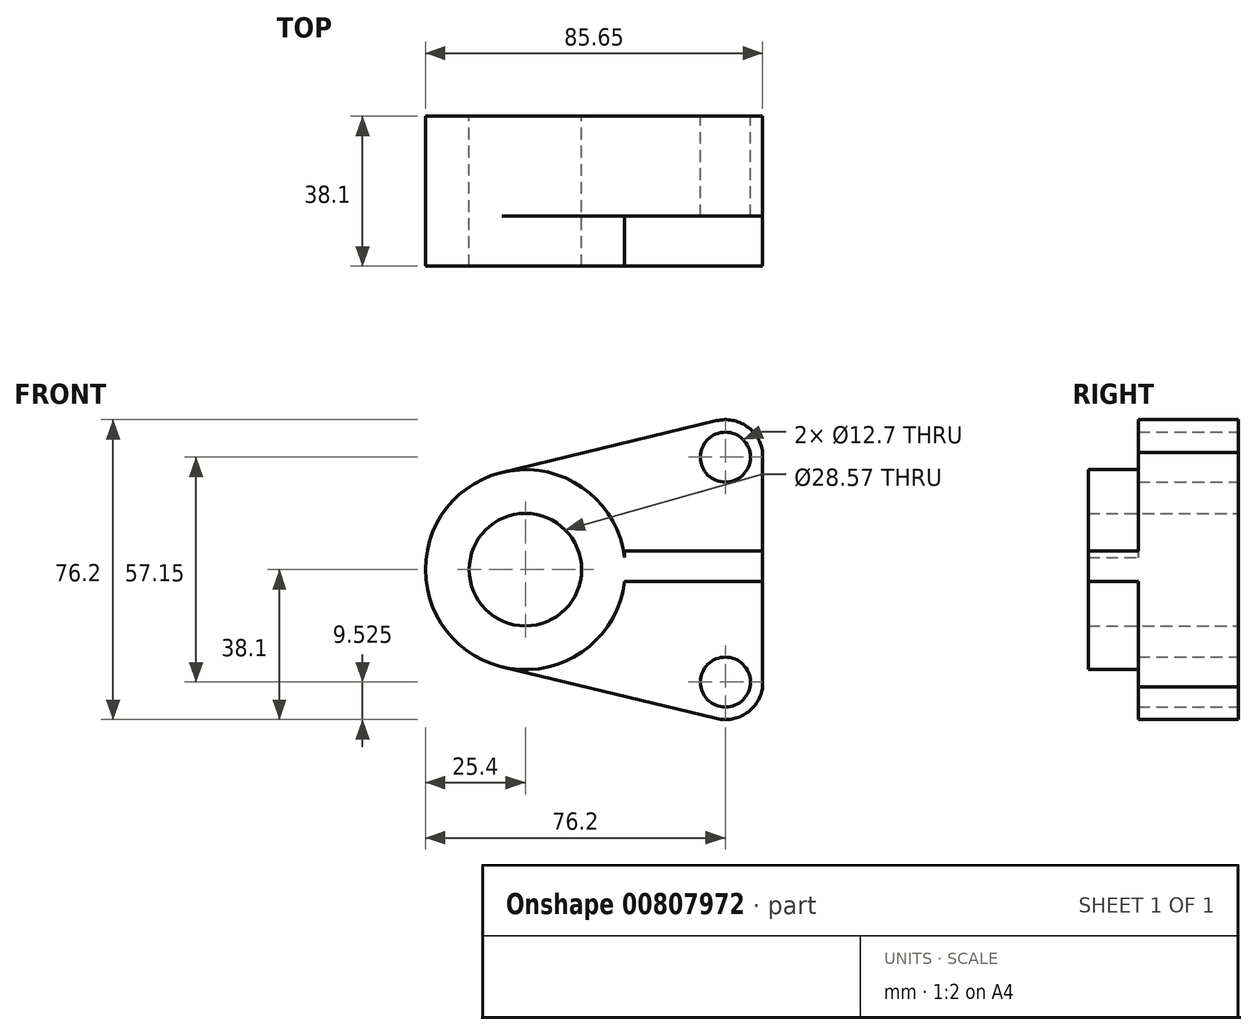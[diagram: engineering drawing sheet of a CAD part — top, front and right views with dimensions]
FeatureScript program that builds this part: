
annotation { "Feature Type Name" : "Feature", "Feature Type Description" : "" }
export const myFeature = defineFeature(function(context is Context, id is Id, definition is map)
    precondition{}
    {
        {
            var Q0;
            Q0=qCreatedBy(makeId("Front.planeOp"),FACE);
            var sketch = newSketch(context, id + "F0", { "sketchPlane" : qUnion([Q0])});
            skCircle(sketch, "E0", {"center": v(0, 0) * mm, "radius": 14.29 * mm});
            skCircle(sketch, "E1", {"center": v(0, 0) * mm, "radius": 25.4 * mm});
            skCircle(sketch, "E2", {"center": v(50.8, -28.58) * mm, "radius": 6.35 * mm});
            skCircle(sketch, "E3", {"center": v(50.8, 28.58) * mm, "radius": 6.35 * mm});
            skArc(sketch, "E4", {"start": v(60.25, 27.4) * mm, "mid": v(57.15, 35.68) * mm, "end": v(48.57, 37.83) * mm});
            skArc(sketch, "E5", {"start": v(48.57, -37.83) * mm, "mid": v(56.22, -36.4) * mm, "end": v(60.25, -29.76) * mm});
            skLineSegment(sketch, "E6", {"start": v(-5.95, -24.7) * mm, "end": v(48.57, -37.83) * mm});
            skLineSegment(sketch, "E7", {"start": v(-5.95, 24.7) * mm, "end": v(48.57, 37.83) * mm});
            skLineSegment(sketch, "E8", {"start": v(60.25, 29.76) * mm, "end": v(60.25, -29.76) * mm});
            skSolve(sketch);
        }
        {
            var Q0;
            Q0=makeQuery(id+"F0.imprint","IMPRINT",FACE,{"disambiguationData":[TD([[makeQuery(id+"F0.imprint","IMPRINT",EDGE,{"derivedFrom":sQuery(id+"F0.wireOp",EDGE,"E2")}),-1.0]])]});
            var Q1;
            Q1=makeQuery(id+"F0.imprint","IMPRINT",FACE,{"disambiguationData":[TD([[makeQuery(id+"F0.imprint","IMPRINT",EDGE,{"derivedFrom":sQuery(id+"F0.wireOp",EDGE,"E0")}),-1.0]])]});
            extrude(context, id + "F1", {"entities" : qUnion([Q0, Q1]), "depth" : 25.4 * mm, "offsetDistance" : 25.4 * mm});
        }
        {
            var Q0;
            Q0=makeQuery(id+"F0.imprint","IMPRINT",FACE,{"disambiguationData":[TD([[makeQuery(id+"F0.imprint","IMPRINT",EDGE,{"derivedFrom":sQuery(id+"F0.wireOp",EDGE,"E0")}),-1.0]])]});
            extrude(context, id + "F2", {"entities" : qUnion([Q0]), "operationType" : NewBodyOperationType.ADD, "depth" : 38.1 * mm, "offsetDistance" : 25.4 * mm});
        }
        {
            var Q0;
            Q0=makeQuery(id+"F1.opExtrude","CAP_FACE",FACE,{"disambiguationData":[OSD([sQuery(id+"F0.wireOp",EDGE,"E0"),sQuery(id+"F0.wireOp",EDGE,"E1"),sQuery(id+"F0.wireOp",EDGE,"E2"),sQuery(id+"F0.wireOp",EDGE,"E3"),sQuery(id+"F0.wireOp",EDGE,"E4"),sQuery(id+"F0.wireOp",EDGE,"E5"),sQuery(id+"F0.wireOp",EDGE,"E6"),sQuery(id+"F0.wireOp",EDGE,"E7"),sQuery(id+"F0.wireOp",EDGE,"E8")])],"isStart":false});
            var sketch = newSketch(context, id + "F3", { "sketchPlane" : qUnion([Q0])});
            skLineSegment(sketch, "E9.bottom", {"start": v(60.25, 4.75) * mm, "end": v(25.22, 4.75) * mm});
            skLineSegment(sketch, "E9.top", {"start": v(60.25, -3.06) * mm, "end": v(25.22, -3.06) * mm});
            skLineSegment(sketch, "E9.left", {"start": v(60.25, 4.75) * mm, "end": v(60.25, -3.06) * mm});
            skLineSegment(sketch, "E9.right", {"start": v(25.22, 4.75) * mm, "end": v(25.22, -3.06) * mm});
            skPoint(sketch, "E10.end.orphan", {"position": v(25.4, 0) * mm});
            skPoint(sketch, "E10.start.orphan", {"position": v(60.25, 0) * mm});
            skSolve(sketch);
        }
        {
            var Q0;
            Q0 = qSketchRegion(id + "F3", true);
            var Q1;
            {var subQ1=sQuery(id+"F3.wireOp",EDGE,"E9.bottom");Q1=makeQuery(id+"F3.imprint","IMPRINT",FACE,{"disambiguationData":[TD([[makeQuery(id+"F3.imprint","IMPRINT",EDGE,{"derivedFrom":subQ1}),1.0]])]});}
            extrude(context, id + "F4", {"entities" : qUnion([Q0, Q1]), "operationType" : NewBodyOperationType.ADD, "depth" : 12.7 * mm, "offsetDistance" : 25.4 * mm});
        }
    });
